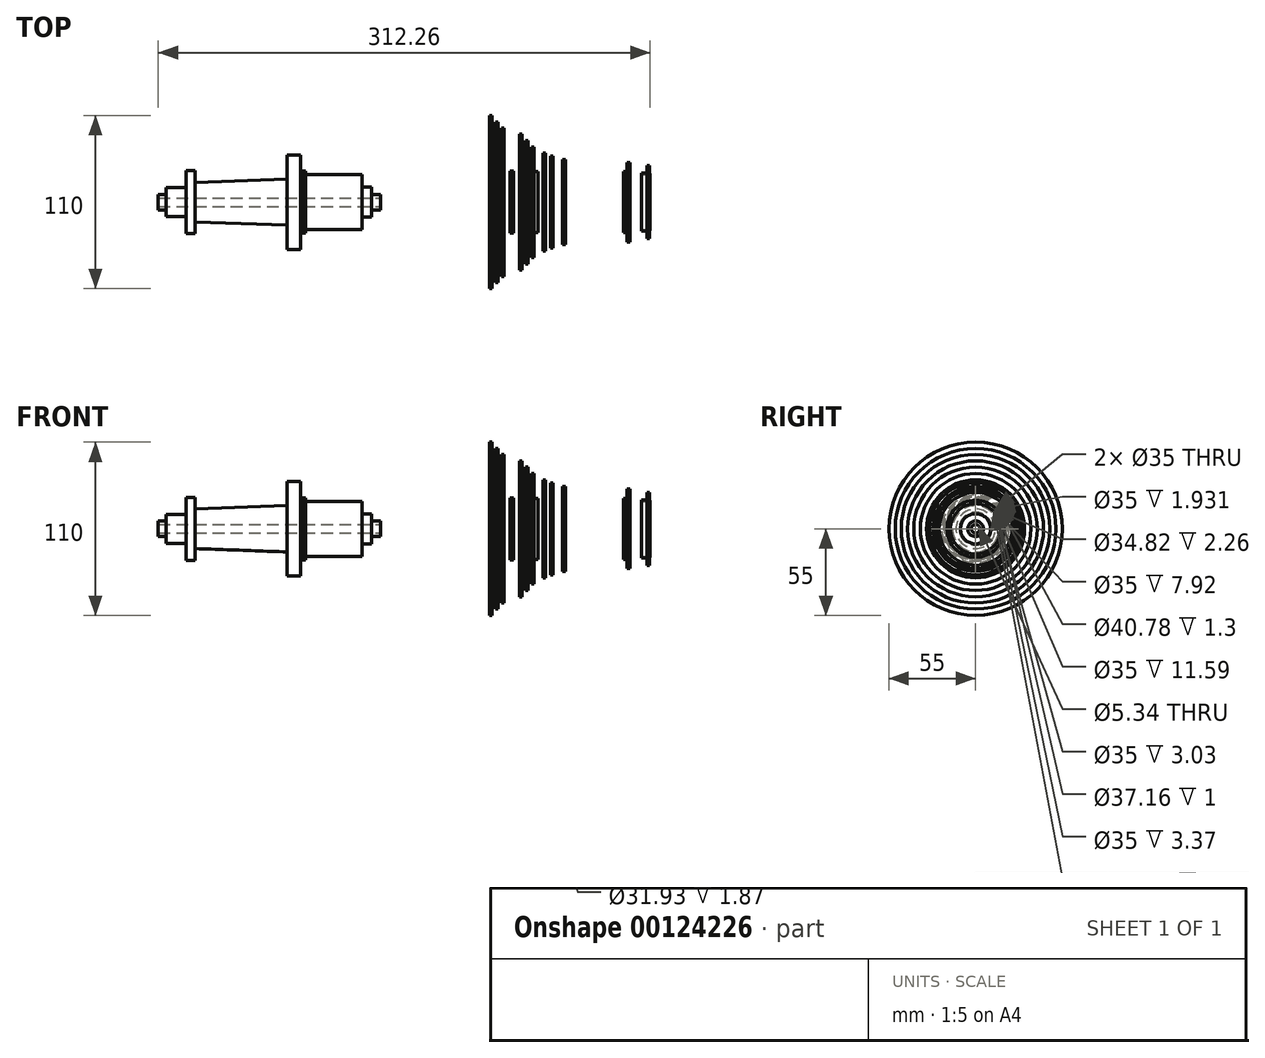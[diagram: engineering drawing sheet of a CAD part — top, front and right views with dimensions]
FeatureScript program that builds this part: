
annotation { "Feature Type Name" : "Feature", "Feature Type Description" : "" }
export const myFeature = defineFeature(function(context is Context, id is Id, definition is map)
    precondition{}
    {
        {
            var Q0;
            Q0=qCreatedBy(makeId("Front.planeOp"),FACE);
            var sketch = newSketch(context, id + "F0", { "sketchPlane" : qUnion([Q0])});
            skLineSegment(sketch, "E0.bottom", {"start": v(-129.8, 4.93) * mm, "end": v(-124.8, 4.93) * mm});
            skLineSegment(sketch, "E0.top", {"start": v(-129.8, 2.67) * mm, "end": v(11.2, 2.67) * mm});
            skLineSegment(sketch, "E0.left", {"start": v(-129.8, 4.93) * mm, "end": v(-129.8, 2.67) * mm});
            skLineSegment(sketch, "E0.right", {"start": v(11.2, 4.93) * mm, "end": v(11.2, 2.67) * mm});
            skLineSegment(sketch, "E1", {"start": v(0, 0) * mm, "end": v(-137.97, 0) * mm});
            skLineSegment(sketch, "E2", {"start": v(5.48, 4.93) * mm, "end": v(5.48, 9.58) * mm});
            skLineSegment(sketch, "E3", {"start": v(5.48, 9.58) * mm, "end": v(-0.42, 9.58) * mm});
            skLineSegment(sketch, "E4", {"start": v(-0.42, 9.58) * mm, "end": v(-0.42, 17.5) * mm});
            skLineSegment(sketch, "E5", {"start": v(-0.42, 17.5) * mm, "end": v(-36.42, 17.5) * mm});
            skLineSegment(sketch, "E6", {"start": v(-36.42, 17.5) * mm, "end": v(-36.42, 19.7) * mm});
            skLineSegment(sketch, "E7", {"start": v(-36.42, 19.7) * mm, "end": v(-38.42, 19.7) * mm});
            skLineSegment(sketch, "E8", {"start": v(-38.42, 19.7) * mm, "end": v(-38.42, 10.43) * mm});
            skLineSegment(sketch, "E9", {"start": v(-38.42, 10.43) * mm, "end": v(-39.42, 10.43) * mm});
            skLineSegment(sketch, "E10", {"start": v(-39.42, 10.43) * mm, "end": v(-39.42, 30) * mm});
            skLineSegment(sketch, "E11", {"start": v(-39.42, 30) * mm, "end": v(-48.08, 30) * mm});
            skLineSegment(sketch, "E12", {"start": v(-48.08, 30) * mm, "end": v(-48.08, 14.7) * mm});
            skLineSegment(sketch, "E13", {"start": v(-48.08, 14.7) * mm, "end": v(-106.36, 12.56) * mm});
            skLineSegment(sketch, "E14", {"start": v(-106.36, 12.56) * mm, "end": v(-106.36, 20) * mm});
            skLineSegment(sketch, "E15", {"start": v(-106.36, 20) * mm, "end": v(-112.05, 20) * mm});
            skLineSegment(sketch, "E16", {"start": v(-112.05, 20) * mm, "end": v(-112.05, 9.2) * mm});
            skLineSegment(sketch, "E17", {"start": v(-112.05, 9.2) * mm, "end": v(-124.8, 9.2) * mm});
            skLineSegment(sketch, "E18", {"start": v(-124.8, 9.2) * mm, "end": v(-124.8, 4.93) * mm});
            skLineSegment(sketch, "E19.trimOffspring", {"start": v(5.48, 4.93) * mm, "end": v(11.2, 4.93) * mm});
            skLineSegment(sketch, "E20", {"start": v(89.66, 17.5) * mm, "end": v(81.74, 17.5) * mm});
            skLineSegment(sketch, "E21", {"start": v(81.74, 17.5) * mm, "end": v(81.74, 20.4) * mm});
            skLineSegment(sketch, "E22", {"start": v(81.74, 20.4) * mm, "end": v(80.44, 20.4) * mm});
            skLineSegment(sketch, "E23", {"start": v(80.44, 20.4) * mm, "end": v(80.44, 55) * mm});
            skLineSegment(sketch, "E24", {"start": v(80.44, 55) * mm, "end": v(82.04, 55) * mm});
            skLineSegment(sketch, "E25", {"start": v(82.04, 55) * mm, "end": v(82.04, 21.39) * mm});
            skLineSegment(sketch, "E26", {"start": v(82.04, 21.39) * mm, "end": v(82.81, 21.39) * mm});
            skLineSegment(sketch, "E27", {"start": v(82.81, 21.39) * mm, "end": v(82.81, 19.16) * mm});
            skLineSegment(sketch, "E28", {"start": v(82.81, 19.16) * mm, "end": v(84.24, 19.16) * mm});
            skLineSegment(sketch, "E29", {"start": v(84.24, 19.16) * mm, "end": v(84.24, 51) * mm});
            skLineSegment(sketch, "E30", {"start": v(84.24, 51) * mm, "end": v(85.86, 51) * mm});
            skLineSegment(sketch, "E31", {"start": v(85.86, 51) * mm, "end": v(85.86, 19.03) * mm});
            skLineSegment(sketch, "E32", {"start": v(85.86, 19.03) * mm, "end": v(88.04, 19.03) * mm});
            skLineSegment(sketch, "E33", {"start": v(88.04, 19.03) * mm, "end": v(88.04, 47.17) * mm});
            skLineSegment(sketch, "E34", {"start": v(88.04, 47.17) * mm, "end": v(89.66, 47.17) * mm});
            skLineSegment(sketch, "E35", {"start": v(89.66, 47.17) * mm, "end": v(89.66, 17.5) * mm});
            skLineSegment(sketch, "E36.bottom", {"start": v(93.47, 19.74) * mm, "end": v(95.73, 19.74) * mm});
            skLineSegment(sketch, "E36.top", {"start": v(93.47, 17.4) * mm, "end": v(95.73, 17.4) * mm});
            skLineSegment(sketch, "E36.left", {"start": v(93.47, 19.74) * mm, "end": v(93.47, 17.4) * mm});
            skLineSegment(sketch, "E36.right", {"start": v(95.73, 19.74) * mm, "end": v(95.73, 17.4) * mm});
            skLineSegment(sketch, "E37.bottom", {"start": v(114.35, 31.09) * mm, "end": v(116, 31.09) * mm});
            skLineSegment(sketch, "E37.top", {"start": v(114.35, 17.5) * mm, "end": v(116, 17.5) * mm});
            skLineSegment(sketch, "E37.left", {"start": v(114.35, 31.09) * mm, "end": v(114.35, 17.5) * mm});
            skLineSegment(sketch, "E37.right", {"start": v(116, 31.09) * mm, "end": v(116, 17.5) * mm});
            skLineSegment(sketch, "E38.bottom", {"start": v(119.25, 29.21) * mm, "end": v(120.9, 29.21) * mm});
            skLineSegment(sketch, "E38.top", {"start": v(119.25, 17.5) * mm, "end": v(120.9, 17.5) * mm});
            skLineSegment(sketch, "E38.left", {"start": v(119.25, 29.21) * mm, "end": v(119.25, 17.5) * mm});
            skLineSegment(sketch, "E38.right", {"start": v(120.9, 29.21) * mm, "end": v(120.9, 17.5) * mm});
            skLineSegment(sketch, "E39.bottom", {"start": v(126.74, 27) * mm, "end": v(128.67, 27) * mm});
            skLineSegment(sketch, "E39.top", {"start": v(126.74, 17.5) * mm, "end": v(128.67, 17.5) * mm});
            skLineSegment(sketch, "E39.left", {"start": v(126.74, 27) * mm, "end": v(126.74, 17.5) * mm});
            skLineSegment(sketch, "E39.right", {"start": v(128.67, 27) * mm, "end": v(128.67, 17.5) * mm});
            skLineSegment(sketch, "E40", {"start": v(111.23, 17.5) * mm, "end": v(99.64, 17.5) * mm});
            skLineSegment(sketch, "E41", {"start": v(99.64, 17.5) * mm, "end": v(99.64, 43.15) * mm});
            skLineSegment(sketch, "E42", {"start": v(99.64, 43.15) * mm, "end": v(101.24, 43.15) * mm});
            skLineSegment(sketch, "E43", {"start": v(101.24, 43.15) * mm, "end": v(101.24, 19.26) * mm});
            skLineSegment(sketch, "E44", {"start": v(101.24, 19.26) * mm, "end": v(103.45, 19.26) * mm});
            skLineSegment(sketch, "E45", {"start": v(103.45, 19.26) * mm, "end": v(103.45, 39.2) * mm});
            skLineSegment(sketch, "E46", {"start": v(103.45, 39.2) * mm, "end": v(105.05, 39.2) * mm});
            skLineSegment(sketch, "E47", {"start": v(105.05, 39.2) * mm, "end": v(105.05, 19.35) * mm});
            skLineSegment(sketch, "E48", {"start": v(105.05, 19.35) * mm, "end": v(107.25, 19.35) * mm});
            skLineSegment(sketch, "E49", {"start": v(107.25, 19.35) * mm, "end": v(107.25, 35.1) * mm});
            skLineSegment(sketch, "E50", {"start": v(107.25, 35.1) * mm, "end": v(108.83, 35.1) * mm});
            skLineSegment(sketch, "E51", {"start": v(108.83, 35.1) * mm, "end": v(108.83, 19.38) * mm});
            skLineSegment(sketch, "E52", {"start": v(108.83, 19.38) * mm, "end": v(111.23, 19.38) * mm});
            skLineSegment(sketch, "E53", {"start": v(111.23, 19.38) * mm, "end": v(111.23, 17.5) * mm});
            skLineSegment(sketch, "E54", {"start": v(180.45, 18.37) * mm, "end": v(180.45, 23.14) * mm});
            skLineSegment(sketch, "E55", {"start": v(180.45, 23.14) * mm, "end": v(182.3, 23.14) * mm});
            skLineSegment(sketch, "E56", {"start": v(182.45, 18.1) * mm, "end": v(182.45, 15.97) * mm});
            skLineSegment(sketch, "E57", {"start": v(182.45, 15.97) * mm, "end": v(180.58, 15.97) * mm});
            skLineSegment(sketch, "E58", {"start": v(177.21, 17.5) * mm, "end": v(177.21, 18.37) * mm});
            skLineSegment(sketch, "E59", {"start": v(177.21, 18.37) * mm, "end": v(180.45, 18.37) * mm});
            skLineSegment(sketch, "E60", {"start": v(167.98, 19.35) * mm, "end": v(167.98, 25.2) * mm});
            skLineSegment(sketch, "E61", {"start": v(167.98, 25.2) * mm, "end": v(169.72, 25.2) * mm});
            skLineSegment(sketch, "E62", {"start": v(169.72, 25.2) * mm, "end": v(169.72, 18.58) * mm});
            skLineSegment(sketch, "E63", {"start": v(168.72, 17.5) * mm, "end": v(165.69, 17.5) * mm});
            skLineSegment(sketch, "E64", {"start": v(165.69, 17.5) * mm, "end": v(165.69, 19.35) * mm});
            skLineSegment(sketch, "E65", {"start": v(165.69, 19.35) * mm, "end": v(167.98, 19.35) * mm});
            skLineSegment(sketch, "E66", {"start": v(0, 0) * mm, "end": v(240.1, 0) * mm});
            skLineSegment(sketch, "E67", {"start": v(169.72, 18.58) * mm, "end": v(168.72, 18.58) * mm});
            skLineSegment(sketch, "E68", {"start": v(168.72, 18.58) * mm, "end": v(168.72, 17.5) * mm});
            skLineSegment(sketch, "E69", {"start": v(177.21, 17.5) * mm, "end": v(180.58, 17.5) * mm});
            skLineSegment(sketch, "E70", {"start": v(180.58, 17.5) * mm, "end": v(180.58, 15.97) * mm});
            skLineSegment(sketch, "E71", {"start": v(182.45, 18.1) * mm, "end": v(182.3, 18.1) * mm});
            skLineSegment(sketch, "E72", {"start": v(182.3, 18.1) * mm, "end": v(182.3, 23.14) * mm});
            skPoint(sketch, "E73.orphan", {"position": v(177.21, 15.97) * mm});
            skPoint(sketch, "E74.orphan", {"position": v(169.72, 17.5) * mm});
            skSolve(sketch);
        }
        {
            var Q0;
            Q0=makeQuery(id+"F0.imprint","IMPRINT",FACE,{"disambiguationData":[TD([[makeQuery(id+"F0.imprint","IMPRINT",EDGE,{"derivedFrom":sQuery(id+"F0.wireOp",EDGE,"E0.bottom")}),-1.0]])]});
            var Q1;
            Q1=sQuery(id+"F0.wireOp",EDGE,"E1");
            revolve(context, id + "F1", {"entities" : qUnion([Q0]), "axis" : qUnion([Q1]), "revolveType" : RevolveType.FULL});
        }
        {
            var Q0;
            Q0=makeQuery(id+"F0.imprint","IMPRINT",FACE,{"disambiguationData":[TD([[makeQuery(id+"F0.imprint","IMPRINT",EDGE,{"derivedFrom":sQuery(id+"F0.wireOp",EDGE,"E20")}),-1.0]])]});
            var Q1;
            Q1=sQuery(id+"F0.wireOp",EDGE,"E1");
            revolve(context, id + "F2", {"entities" : qUnion([Q0]), "axis" : qUnion([Q1]), "revolveType" : RevolveType.FULL});
        }
        {
            var Q0;
            Q0=makeQuery(id+"F0.imprint","IMPRINT",FACE,{"disambiguationData":[TD([[makeQuery(id+"F0.imprint","IMPRINT",EDGE,{"derivedFrom":sQuery(id+"F0.wireOp",EDGE,"E40")}),-1.0]])]});
            var Q1;
            Q1=sQuery(id+"F0.wireOp",EDGE,"E1");
            revolve(context, id + "F3", {"entities" : qUnion([Q0]), "axis" : qUnion([Q1]), "revolveType" : RevolveType.FULL});
        }
        {
            var Q0;
            Q0=makeQuery(id+"F0.imprint","IMPRINT",FACE,{"disambiguationData":[TD([[makeQuery(id+"F0.imprint","IMPRINT",EDGE,{"derivedFrom":sQuery(id+"F0.wireOp",EDGE,"E36.bottom")}),-1.0]])]});
            var Q1;
            Q1=sQuery(id+"F0.wireOp",EDGE,"E1");
            revolve(context, id + "F4", {"entities" : qUnion([Q0]), "axis" : qUnion([Q1]), "revolveType" : RevolveType.FULL});
        }
        {
            var Q0;
            Q0=makeQuery(id+"F0.imprint","IMPRINT",FACE,{"disambiguationData":[TD([[makeQuery(id+"F0.imprint","IMPRINT",EDGE,{"derivedFrom":sQuery(id+"F0.wireOp",EDGE,"E37.bottom")}),-1.0]])]});
            var Q1;
            Q1=sQuery(id+"F0.wireOp",EDGE,"E1");
            revolve(context, id + "F5", {"entities" : qUnion([Q0]), "axis" : qUnion([Q1]), "revolveType" : RevolveType.FULL});
        }
        {
            var Q0;
            Q0=makeQuery(id+"F0.imprint","IMPRINT",FACE,{"disambiguationData":[TD([[makeQuery(id+"F0.imprint","IMPRINT",EDGE,{"derivedFrom":sQuery(id+"F0.wireOp",EDGE,"E38.bottom")}),-1.0]])]});
            var Q1;
            Q1=sQuery(id+"F0.wireOp",EDGE,"E1");
            revolve(context, id + "F6", {"entities" : qUnion([Q0]), "axis" : qUnion([Q1]), "revolveType" : RevolveType.FULL});
        }
        {
            var Q0;
            Q0=makeQuery(id+"F0.imprint","IMPRINT",FACE,{"disambiguationData":[TD([[makeQuery(id+"F0.imprint","IMPRINT",EDGE,{"derivedFrom":sQuery(id+"F0.wireOp",EDGE,"E39.bottom")}),-1.0]])]});
            var Q1;
            Q1=sQuery(id+"F0.wireOp",EDGE,"E1");
            revolve(context, id + "F7", {"entities" : qUnion([Q0]), "axis" : qUnion([Q1]), "revolveType" : RevolveType.FULL});
        }
        {
            var Q0;
            Q0=makeQuery(id+"F0.imprint","IMPRINT",FACE,{"disambiguationData":[TD([[makeQuery(id+"F0.imprint","IMPRINT",EDGE,{"derivedFrom":sQuery(id+"F0.wireOp",EDGE,"E60")}),-1.0]])]});
            var Q1;
            Q1=sQuery(id+"F0.wireOp",EDGE,"E1");
            revolve(context, id + "F8", {"entities" : qUnion([Q0]), "axis" : qUnion([Q1]), "revolveType" : RevolveType.FULL});
        }
        {
            var Q0;
            Q0=makeQuery(id+"F0.imprint","IMPRINT",FACE,{"disambiguationData":[TD([[makeQuery(id+"F0.imprint","IMPRINT",EDGE,{"derivedFrom":sQuery(id+"F0.wireOp",EDGE,"E54")}),-1.0]])]});
            var Q1;
            Q1=sQuery(id+"F0.wireOp",EDGE,"E1");
            revolve(context, id + "F9", {"entities" : qUnion([Q0]), "axis" : qUnion([Q1]), "revolveType" : RevolveType.FULL});
        }
    });
